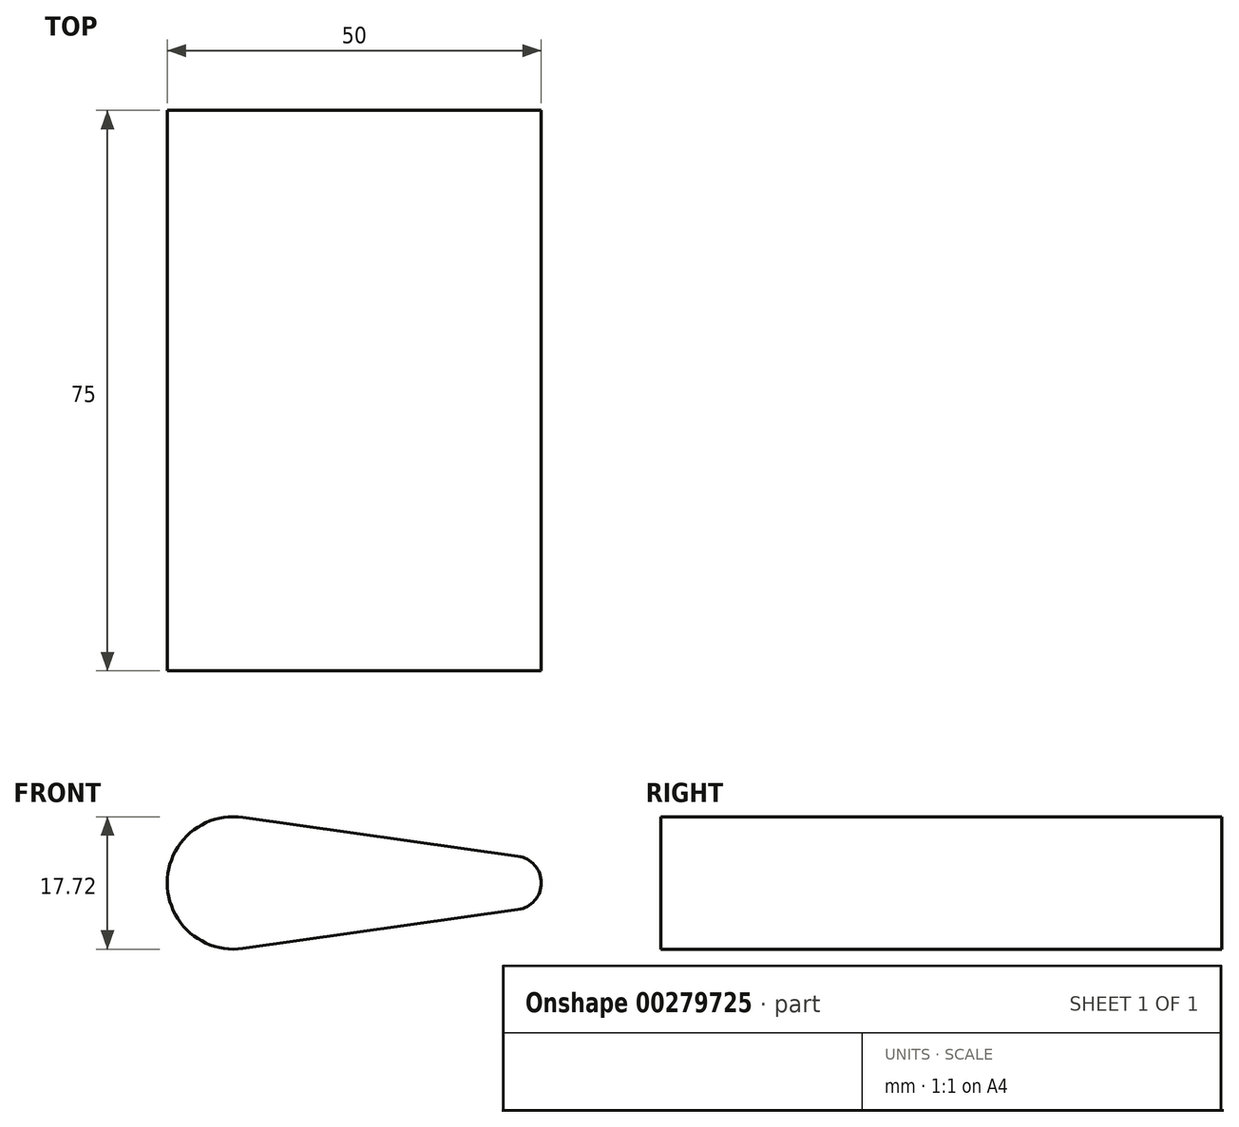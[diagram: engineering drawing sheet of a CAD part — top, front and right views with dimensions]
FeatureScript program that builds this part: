
annotation { "Feature Type Name" : "Feature", "Feature Type Description" : "" }
export const myFeature = defineFeature(function(context is Context, id is Id, definition is map)
    precondition{}
    {
        {
            var Q0;
            Q0=qCreatedBy(makeId("Front.planeOp"),FACE);
            var sketch = newSketch(context, id + "F0", { "sketchPlane" : qUnion([Q0])});
            skCircle(sketch, "E0", {"center": v(-25.95, 0) * mm, "radius": 8.86 * mm});
            skCircle(sketch, "E1", {"center": v(11.58, 0) * mm, "radius": 3.6 * mm});
            skLineSegment(sketch, "E2", {"start": v(-24.71, 8.77) * mm, "end": v(12.08, 3.57) * mm});
            skLineSegment(sketch, "E3", {"start": v(-24.71, -8.77) * mm, "end": v(12.08, -3.57) * mm});
            skSolve(sketch);
        }
        {
            var Q0;
            {var subQ0=sQuery(id+"F0.wireOp",EDGE,"E2");Q0=makeQuery(id+"F0.imprint","IMPRINT",FACE,{"disambiguationData":[TD([[makeQuery(id+"F0.imprint","IMPRINT",EDGE,{"derivedFrom":subQ0}),-1.0]])]});}
            var Q1;
            {var subQ0=sQuery(id+"F0.wireOp",EDGE,"E0");var subQ1=makeQuery(id+"F0.imprint","INTERSECT",VERTEX,{"derivedFrom":[subQ0,sQuery(id+"F0.wireOp",EDGE,"E2")]});Q1=makeQuery(id+"F0.imprint","IMPRINT",FACE,{"disambiguationData":[TD([[makeQuery(id+"F0.imprint","IMPRINT",EDGE,{"disambiguationData":[TD([[subQ1,-1.0]])],"derivedFrom":subQ0}),1.0]])]});}
            var Q2;
            {var subQ0=sQuery(id+"F0.wireOp",EDGE,"E1");var subQ1=makeQuery(id+"F0.imprint","INTERSECT",VERTEX,{"derivedFrom":[subQ0,sQuery(id+"F0.wireOp",EDGE,"E2")]});Q2=makeQuery(id+"F0.imprint","IMPRINT",FACE,{"disambiguationData":[TD([[makeQuery(id+"F0.imprint","IMPRINT",EDGE,{"disambiguationData":[TD([[subQ1,-1.0]])],"derivedFrom":subQ0}),1.0]])]});}
            extrude(context, id + "F1", {"entities" : qUnion([Q0, Q1, Q2]), "depth" : 75 * mm});
        }
    });
